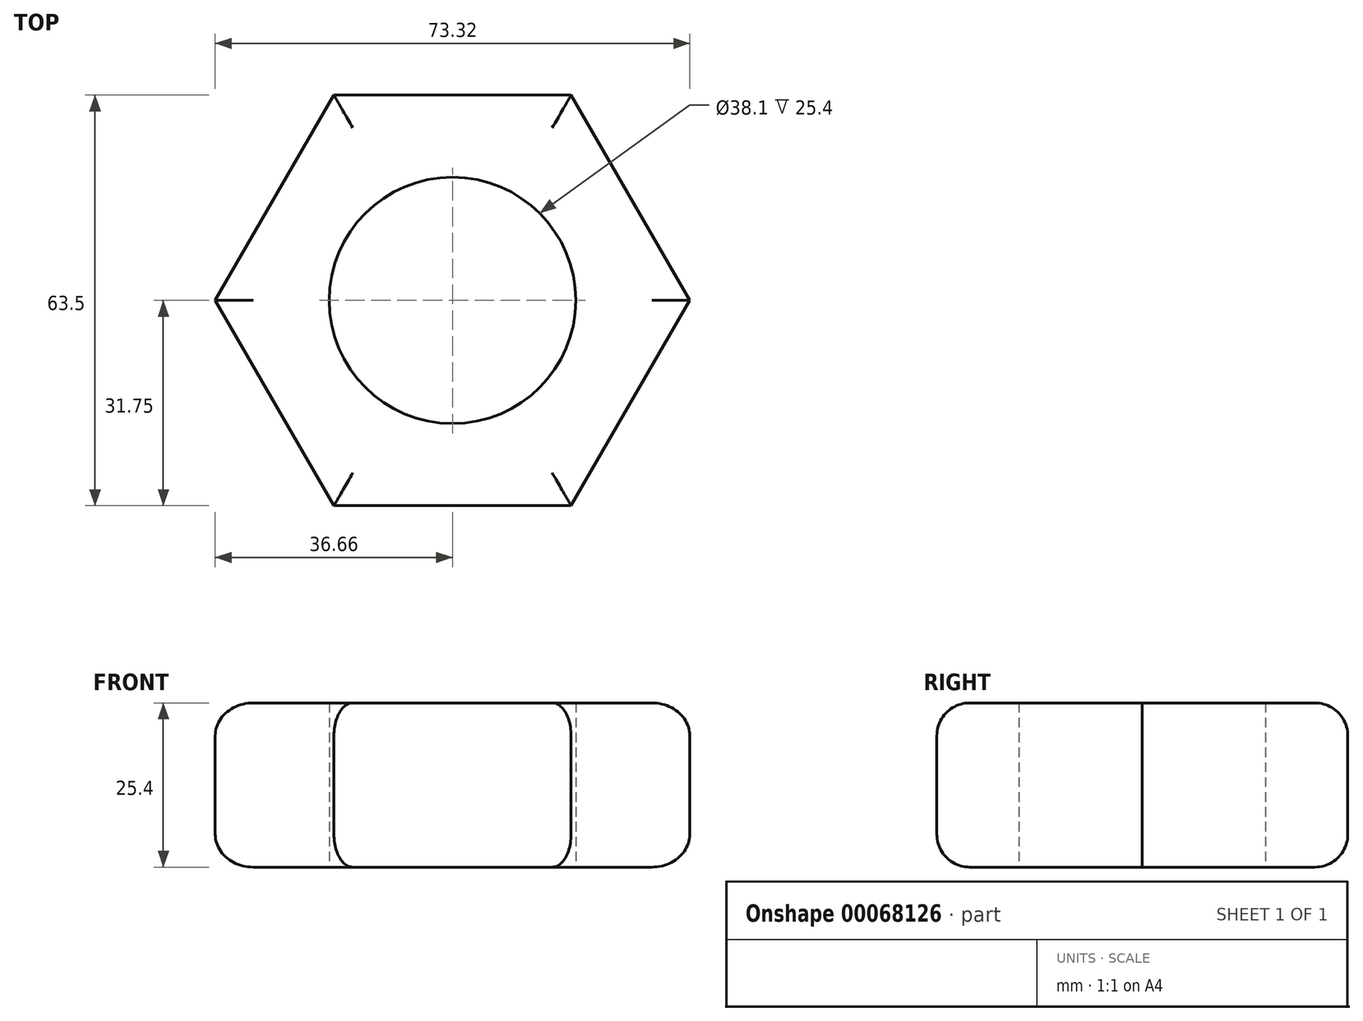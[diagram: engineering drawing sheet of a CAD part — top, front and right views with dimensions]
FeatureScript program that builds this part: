
annotation { "Feature Type Name" : "Feature", "Feature Type Description" : "" }
export const myFeature = defineFeature(function(context is Context, id is Id, definition is map)
    precondition{}
    {
        {
            var Q0;
            Q0=qCreatedBy(makeId("Top.planeOp"),FACE);
            var sketch = newSketch(context, id + "F0", { "sketchPlane" : qUnion([Q0])});
            skCircle(sketch, "E0.cCircle", {"center": v(0, 0) * mm, "radius": 31.75 * mm, "construction": true});
            skLineSegment(sketch, "E0.0", {"start": v(36.66, 0) * mm, "end": v(18.33, -31.75) * mm});
            skLineSegment(sketch, "E0.1", {"start": v(18.33, -31.75) * mm, "end": v(-18.33, -31.75) * mm});
            skLineSegment(sketch, "E0.2", {"start": v(-18.33, -31.75) * mm, "end": v(-36.66, 0) * mm});
            skLineSegment(sketch, "E0.3", {"start": v(-36.66, 0) * mm, "end": v(-18.33, 31.75) * mm});
            skLineSegment(sketch, "E0.4", {"start": v(-18.33, 31.75) * mm, "end": v(18.33, 31.75) * mm});
            skLineSegment(sketch, "E0.5", {"start": v(18.33, 31.75) * mm, "end": v(36.66, 0) * mm});
            skPoint(sketch, "E0.0.midPoint", {"position": v(27.5, -15.88) * mm});
            skCircle(sketch, "E1", {"center": v(0, 0) * mm, "radius": 19.05 * mm});
            skSolve(sketch);
        }
        {
            var Q0;
            Q0 = qSketchRegion(id + "F0", true);
            extrude(context, id + "F1", {"entities" : qUnion([Q0]), "depth" : 25.4 * mm});
        }
        {
            var Q0;
            Q0=makeQuery(id+"F1.opExtrude","CAP_EDGE",EDGE,{"disambiguationData":[OSD([sQuery(id+"F0.wireOp",EDGE,"E0.2")])],"isStart":false});
            var Q1;
            Q1=makeQuery(id+"F1.opExtrude","CAP_EDGE",EDGE,{"disambiguationData":[OSD([sQuery(id+"F0.wireOp",EDGE,"E0.1")])],"isStart":false});
            var Q2;
            Q2=makeQuery(id+"F1.opExtrude","CAP_EDGE",EDGE,{"disambiguationData":[OSD([sQuery(id+"F0.wireOp",EDGE,"E0.0")])],"isStart":false});
            var Q3;
            Q3=makeQuery(id+"F1.opExtrude","CAP_EDGE",EDGE,{"disambiguationData":[OSD([sQuery(id+"F0.wireOp",EDGE,"E0.5")])],"isStart":false});
            var Q4;
            Q4=makeQuery(id+"F1.opExtrude","CAP_EDGE",EDGE,{"disambiguationData":[OSD([sQuery(id+"F0.wireOp",EDGE,"E0.4")])],"isStart":false});
            var Q5;
            Q5=makeQuery(id+"F1.opExtrude","CAP_EDGE",EDGE,{"disambiguationData":[OSD([sQuery(id+"F0.wireOp",EDGE,"E0.3")])],"isStart":false});
            var Q6;
            Q6=makeQuery(id+"F1.opExtrude","CAP_EDGE",EDGE,{"disambiguationData":[OSD([sQuery(id+"F0.wireOp",EDGE,"E0.3")])],"isStart":true});
            var Q7;
            Q7=makeQuery(id+"F1.opExtrude","CAP_EDGE",EDGE,{"disambiguationData":[OSD([sQuery(id+"F0.wireOp",EDGE,"E0.4")])],"isStart":true});
            var Q8;
            Q8=makeQuery(id+"F1.opExtrude","CAP_EDGE",EDGE,{"disambiguationData":[OSD([sQuery(id+"F0.wireOp",EDGE,"E0.5")])],"isStart":true});
            var Q9;
            Q9=makeQuery(id+"F1.opExtrude","CAP_EDGE",EDGE,{"disambiguationData":[OSD([sQuery(id+"F0.wireOp",EDGE,"E0.0")])],"isStart":true});
            var Q10;
            Q10=makeQuery(id+"F1.opExtrude","CAP_EDGE",EDGE,{"disambiguationData":[OSD([sQuery(id+"F0.wireOp",EDGE,"E0.1")])],"isStart":true});
            var Q11;
            Q11=makeQuery(id+"F1.opExtrude","CAP_EDGE",EDGE,{"disambiguationData":[OSD([sQuery(id+"F0.wireOp",EDGE,"E0.2")])],"isStart":true});
            fillet(context, id + "F2", {"entities" : qUnion([Q0, Q1, Q2, Q3, Q4, Q5, Q6, Q7, Q8, Q9, Q10, Q11]), "radius" : 5.08 * mm, "tangentPropagation" : true, "allowEdgeOverflow" : false});
        }
    });
